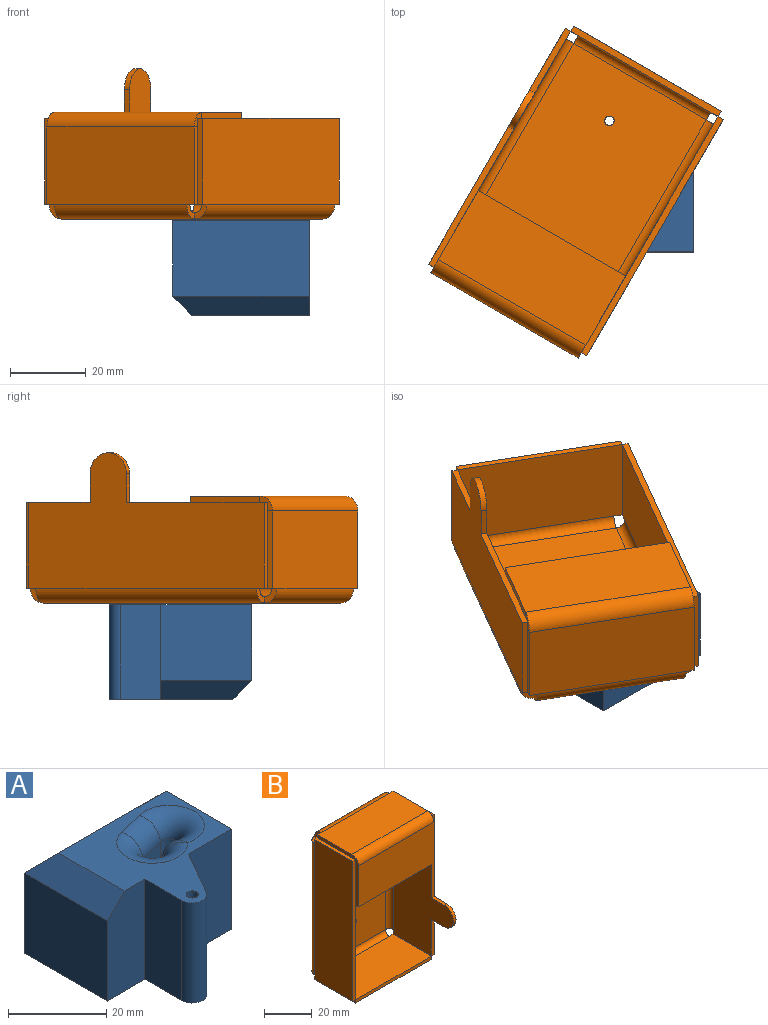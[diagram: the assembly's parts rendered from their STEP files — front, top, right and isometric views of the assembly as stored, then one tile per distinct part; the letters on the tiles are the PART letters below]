
ASSEMBLY  parts=2 mates=1
PART A: 27 faces, bbox 39.4x37.6x25 mm
  f0: plane 32.62x31mm, normal (0,0,1), area 437.7mm2, adj f2,f3,f4,f5,f6,f7,f10,f11
  f1: plane 24x20mm, normal (-1,0,0), area 480mm2, adj f2,f8,f9,f11
  f2: plane 25x10.89mm, normal (0,-1,0), area 259.8mm2, adj f0,f1,f3,f9,f11
  f3: plane 25x10.62mm, normal (-1,0,0), area 265.4mm2, adj f0,f2,f4,f9
  f4: cylinder r=3mm len=25mm, axis (0,0,-1), area 196.3mm2, adj f0,f3,f5,f9
  f5: plane 25x12.12mm, normal (0.87,-0.5,0), area 349.8mm2, adj f0,f4,f6,f9
  f6: plane 25x12.51mm, normal (0,-1,0), area 312.8mm2, adj f0,f5,f7,f9
  f7: plane 25x24mm, normal (1,0,0), area 542.9mm2, adj f0,f6,f8,f9,f12,f22,f23,f24
  f8: plane 36x20mm, normal (0,1,0), area 720mm2, adj f1,f7,f9,f12
  f9: plane 37.62x36mm, normal (0,0,-1), area 974.6mm2, adj f1,f2,f3,f4,f5,f6,f7,f8
  f10: cylinder r=1.25mm len=25mm, axis (0,0,1), area 196.3mm2, adj f0,f9
  f11: plane 24x5mm, normal (-0.71,0,0.71), area 152mm2, adj f0,f1,f2,f12
  f12: plane 36x5mm, normal (0,0.71,0.71), area 236.9mm2, adj f0,f7,f8,f11
  f13: cylinder r=2.26mm len=7mm, axis (0,0,1), area 28.5mm2, adj f14,f16,f17,f18
  f14: cylinder r=2.15mm len=7mm, axis (0,0,1), area 60.4mm2, adj f13,f15,f17,f19
  f15: plane 7x6.79mm, normal (0.25,-0.97,0), area 49mm2, adj f14,f16,f17,f21
  f16: cylinder r=2.26mm len=7mm, axis (0,0,1), area 64.4mm2, adj f13,f15,f17,f20
  f17: plane 11.17x6.24mm, normal (0,0,1), area 40.2mm2, adj f13,f14,f15,f16
  f18: bspline ~6.89x6.44mm, area 18.4mm2, adj f13,f19,f20
  f19: torus R=7.15mm, axis (0,0,1), area 118mm2, adj f0,f14,f18,f21
  f20: torus R=7.26mm, axis (0,0,1), area 123.1mm2, adj f0,f16,f18,f21
  f21: cylinder r=5mm len=8.01mm, axis (0.97,0.25,0), area 55mm2, adj f0,f15,f19,f20
  f22: extruded ~14.24x12.27mm, area 107.1mm2, adj f7,f23,f25,f26
  f23: cylinder r=1mm len=5mm, axis (1,0,0), area 15.7mm2, adj f7,f22,f24,f26
  f24: extruded ~12.93x11.98mm, area 100.4mm2, adj f7,f23,f25,f26
  f25: cylinder r=1mm len=5mm, axis (1,0,0), area 15.7mm2, adj f7,f22,f24,f26
  f26: plane 15.58x14.13mm, normal (1,0,0), area 44.6mm2, adj f22,f23,f24,f25
PART B: 59 faces, bbox 48.2x39.7x75.2 mm
  f0: plane 2.28x1.6mm, normal (0,1,0), area 3.6mm2, adj f1,f4,f5,f45
  f1: plane 20.4x1.6mm, normal (1,0,0), area 32.6mm2, adj f0,f4,f5,f54
  f2: plane 2.28x1.6mm, normal (0,1,0), area 3.6mm2, adj f3,f4,f5,f46
  f3: plane 20.4x1.6mm, normal (-1,0,0), area 32.6mm2, adj f2,f4,f5,f55
  f4: plane 44.96x20.4mm, normal (0,0,1), area 917.2mm2, adj f0,f1,f2,f3,f47,f56
  f5: plane 44.96x20.4mm, normal (0,0,-1), area 917.2mm2, adj f0,f1,f2,f3,f48,f57
  f6: plane 67.4x40.4mm, normal (0,1,0), area 2718.1mm2, adj f17,f28,f43,f47,f58
  f7: plane 67.4x40.4mm, normal (0,-1,0), area 2718.1mm2, adj f18,f29,f44,f48,f58
  f8: plane 2.28x1.6mm, normal (0,1,0), area 3.6mm2, adj f10,f13,f14,f16
  f9: plane 44.96x1.6mm, normal (0,-1,0), area 71.9mm2, adj f10,f12,f13,f14
  f10: plane 22.7x1.6mm, normal (-1,0,0), area 36.3mm2, adj f8,f9,f13,f14
  f11: plane 2.28x1.6mm, normal (0,1,0), area 3.6mm2, adj f12,f13,f14,f15
  f12: plane 22.7x1.6mm, normal (1,0,0), area 36.3mm2, adj f9,f11,f13,f14
  f13: plane 44.96x22.7mm, normal (0,0,-1), area 1020.6mm2, adj f8,f9,f10,f11,f12,f17
  f14: plane 44.96x22.7mm, normal (0,0,1), area 1020.6mm2, adj f8,f9,f10,f11,f12,f18
  f15: plane 3.9x3.9mm, normal (1,0,0), area 7.8mm2, adj f11,f17,f18,f41
  f16: plane 3.9x3.9mm, normal (-1,0,0), area 7.8mm2, adj f8,f17,f18,f26
  f17: cylinder r=3.9mm len=40.4mm, axis (1,0,0), area 247.5mm2, adj f6,f13,f15,f16
  f18: cylinder r=2.3mm len=40.4mm, axis (1,0,0), area 146mm2, adj f7,f14,f15,f16
  f19: plane 2.28x1.6mm, normal (0,1,0), area 3.6mm2, adj f21,f24,f25,f27
  f20: plane 71.96x1.6mm, normal (0,-1,0), area 115.1mm2, adj f21,f23,f24,f25
  f21: plane 22.7x1.6mm, normal (0,0,1), area 36.3mm2, adj f19,f20,f24,f25
  f22: plane 2.28x1.6mm, normal (0,1,0), area 3.6mm2, adj f23,f24,f25,f26
  f23: plane 22.7x1.6mm, normal (0,0,-1), area 36.3mm2, adj f20,f22,f24,f25
  f24: plane 71.96x22.7mm, normal (-1,0,0), area 1633.5mm2, adj f19,f20,f21,f22,f23,f28
  f25: plane 71.96x22.7mm, normal (1,0,0), area 1633.5mm2, adj f19,f20,f21,f22,f23,f29
  f26: plane 3.9x3.9mm, normal (0,0,-1), area 7.8mm2, adj f16,f22,f28,f29
  f27: plane 3.9x3.9mm, normal (0,0,1), area 7.8mm2, adj f19,f28,f29,f46
  f28: cylinder r=3.9mm len=67.4mm, axis (0,0,-1), area 412.9mm2, adj f6,f24,f26,f27
  f29: cylinder r=2.3mm len=67.4mm, axis (0,0,-1), area 243.5mm2, adj f7,f25,f26,f27
  f30: plane 2.28x1.6mm, normal (0,1,0), area 3.6mm2, adj f36,f39,f40,f41
  f31: plane 42x1.6mm, normal (0,-1,0), area 67.2mm2, adj f32,f38,f39,f40
  f32: plane 7.52x1.6mm, normal (0,0,1), area 12mm2, adj f31,f33,f39,f40
  f33: cylinder r=5.56mm len=11.11mm, axis (1,0,0), area 27.9mm2, adj f32,f34,f39,f40
  f34: plane 7.52x1.6mm, normal (0,0,-1), area 12mm2, adj f33,f35,f39,f40
  f35: plane 18.84x1.6mm, normal (0,-1,0), area 30.1mm2, adj f34,f36,f39,f40
  f36: plane 22.7x1.6mm, normal (0,0,-1), area 36.3mm2, adj f30,f35,f39,f40
  f37: plane 2.28x1.6mm, normal (0,1,0), area 3.6mm2, adj f38,f39,f40,f42
  f38: plane 22.7x1.6mm, normal (0,0,1), area 36.3mm2, adj f31,f37,f39,f40
  f39: plane 71.96x35.78mm, normal (1,0,0), area 1765.6mm2, adj f30,f31,f32,f33,f34,f35,f36,f37
  f40: plane 71.96x35.78mm, normal (-1,0,0), area 1765.6mm2, adj f30,f31,f32,f33,f34,f35,f36,f37
  f41: plane 3.9x3.9mm, normal (0,0,-1), area 7.8mm2, adj f15,f30,f43,f44
  f42: plane 3.9x3.9mm, normal (0,0,1), area 7.8mm2, adj f37,f43,f44,f45
  f43: cylinder r=3.9mm len=67.4mm, axis (0,0,-1), area 412.9mm2, adj f6,f39,f41,f42
  f44: cylinder r=2.3mm len=67.4mm, axis (0,0,-1), area 243.5mm2, adj f7,f40,f41,f42
  f45: plane 3.9x3.9mm, normal (1,0,0), area 7.8mm2, adj f0,f42,f47,f48
  f46: plane 3.9x3.9mm, normal (-1,0,0), area 7.8mm2, adj f2,f27,f47,f48
  f47: cylinder r=3.9mm len=40.4mm, axis (1,0,0), area 247.5mm2, adj f4,f6,f45,f46
  f48: cylinder r=2.3mm len=40.4mm, axis (1,0,0), area 146mm2, adj f5,f7,f45,f46
  f49: plane 44.96x1.6mm, normal (0,0,-1), area 71.9mm2, adj f50,f51,f52,f53
  f50: plane 21.1x1.6mm, normal (1,0,0), area 33.8mm2, adj f49,f52,f53,f54
  f51: plane 21.1x1.6mm, normal (-1,0,0), area 33.8mm2, adj f49,f52,f53,f55
  f52: plane 44.96x21.1mm, normal (0,-1,0), area 948.7mm2, adj f49,f50,f51,f56
  f53: plane 44.96x21.1mm, normal (0,1,0), area 948.7mm2, adj f49,f50,f51,f57
  f54: plane 3.9x3.9mm, normal (1,0,0), area 7.8mm2, adj f1,f50,f56,f57
  f55: plane 3.9x3.9mm, normal (-1,0,0), area 7.8mm2, adj f3,f51,f56,f57
  f56: cylinder r=3.9mm len=44.96mm, axis (1,0,0), area 275.4mm2, adj f4,f52,f54,f55
  f57: cylinder r=2.3mm len=44.96mm, axis (1,0,0), area 162.4mm2, adj f5,f53,f54,f55
  f58: cylinder r=1.25mm len=2.5mm, axis (0,-1,0), area 12.6mm2, adj f6,f7
PLACE A rot(axis=(1,0,0),180deg) t=(4.11,-22.62,0)mm fixed
PLACE B rot(axis=(-0.19,-0.69,0.69),158.9deg) t=(-9.43,-19.89,2)mm
MATE revolute A.f4 <-> B.f58  axis (0,0,1) through (0,0,0)mm
